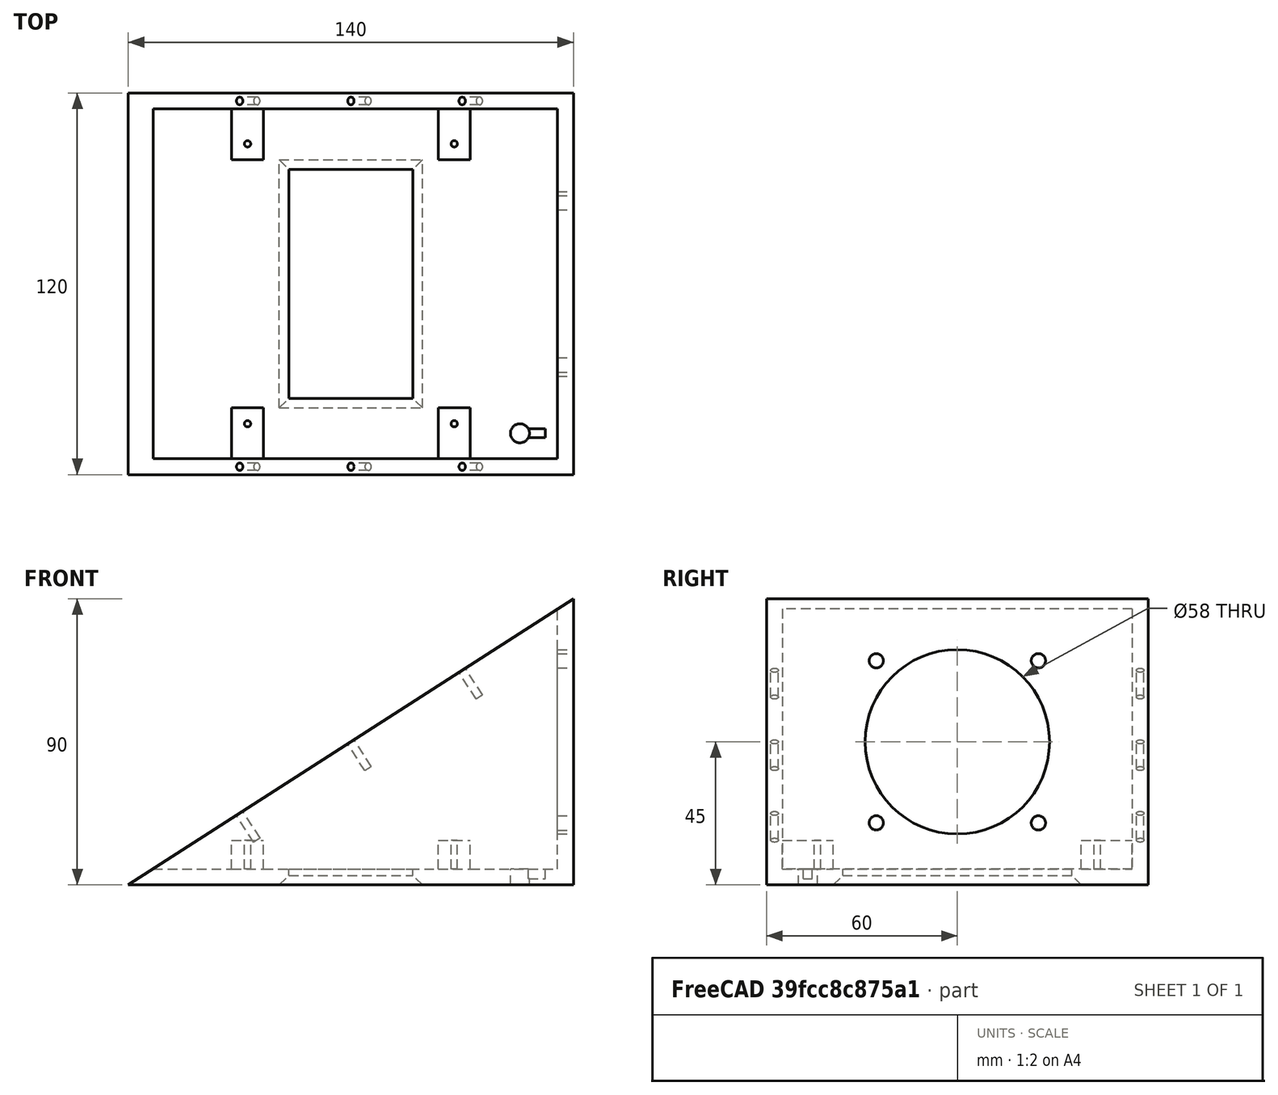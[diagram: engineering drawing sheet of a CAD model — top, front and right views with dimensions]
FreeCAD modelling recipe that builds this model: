
FCSTD DOCUMENT  (FreeCAD 0.19R22284 (Git))
Label: lcdmount
License: All rights reserved
LicenseURL: http://en.wikipedia.org/wiki/All_rights_reserved
objects: Part::Box×6, Part::Cylinder×5, Part::Cut×5, Part::MultiFuse×5, Part::Wedge×4, Part::FeaturePython×3, Sketcher::SketchObject×1, Spreadsheet::Sheet×1, Part::Chamfer×1, Mesh::Feature×1
note: 30 computed .brp shape members not serialized (recipe doc carries the construction recipe); baked Part::Feature solids carry a one-line shape summary decoded from their .brp

FEATURE [Sketcher::SketchObject] Sketch
  sketch-geometry (8):
    g0: LineSegment StartX=31.035 StartY=30.82 StartZ=0 EndX=-31.035 EndY=30.82 EndZ=0
    g1: LineSegment StartX=-31.035 StartY=30.82 StartZ=0 EndX=-31.035 EndY=-30.82 EndZ=0
    g2: LineSegment StartX=-31.035 StartY=-30.82 StartZ=0 EndX=31.035 EndY=-30.82 EndZ=0
    g3: LineSegment StartX=31.035 StartY=-30.82 StartZ=0 EndX=31.035 EndY=30.82 EndZ=0
    g4: LineSegment [constr] StartX=-21.915 StartY=21.365 StartZ=0 EndX=21.915 EndY=21.365 EndZ=0
    g5: LineSegment [constr] StartX=21.915 StartY=21.365 StartZ=0 EndX=21.915 EndY=-21.365 EndZ=0
    g6: LineSegment [constr] StartX=21.915 StartY=-21.365 StartZ=0 EndX=-21.915 EndY=-21.365 EndZ=0
    g7: LineSegment [constr] StartX=-21.915 StartY=-21.365 StartZ=0 EndX=-21.915 EndY=21.365 EndZ=0
  constraints (21):
    c: Coincident(g0,g1)
    c: Coincident(g1,g2)
    c: Coincident(g2,g3)
    c: Coincident(g3,g0)
    c: Horizontal(g0)
    c: Horizontal(g2)
    c: Vertical(g1)
    c: Vertical(g3)
    c: DistanceX(g0,g0) = 62.07  'extSizeX'
    c: DistanceY(g1,g1) = 61.64  'extSizeY'
    c: Symmetric(g0,g2,g-1)
    c: Coincident(g4,g5)
    c: Coincident(g5,g6)
    c: Coincident(g6,g7)
    c: Coincident(g7,g4)
    c: Horizontal(g4)
    c: Horizontal(g6)
    c: Vertical(g5)
    c: Vertical(g7)
    c: DistanceX(g4,g4) = 43.83  'LCDHoleOffsetX'
    c: DistanceY(g7,g7) = 42.73  'LCDHoleOffsetY'
FEATURE [Part::Box] Box001  label="lcdhole"
  AttacherType = Attacher::AttachEngine3D
  Height = 5
  Length = 39
  Placement = pos=(-19.5,-36,0) rot=(0,0,1;0rad)
  Width = 72
  expr: Height = Spreadsheet.mountThickness
  expr: Length = Spreadsheet.LCDSizeX
  expr: Width = Spreadsheet.LCDSizeY
  expr: .Placement.Base.x = Length / -2
  expr: .Placement.Base.y = Width / -2
FEATURE [Spreadsheet::Sheet] Spreadsheet
  cells = C2=X; D2=Y; E2=Z; B3=LCDSize; C3(LCDSizeX)==39mm; D3(LCDSizeY)==72mm; E3(LCDSizeZ)==9mm; B4=MountSize; C4(MountSizeX)==140mm; D4(MountSizeY)==110mm; A5=Position of mouting holes on LCD board; B5=LCDHoleOffset; C5(LCDHoleOffsetX)==65mm; D5(LCDHoleOffsetY)==88mm; B6=MountThickness; F6(mountThickness)==5mm; A7=Size of hole for the LCD screws; B7=LCDScrewHoleSize; F7(LCDScrewHoleSize)==1mm; A8=Size of the cylider the LCD will rest on top of, containing the screw hole; B8=LCDScrewHoleMountSize; F8(LCDScrewHoleMountSize)==5mm; A9=Length of the back part, when the fan mounts; B9=backLength; F9(backLength)==90mm; B10=angleA; G10(angleA)==atan(backLength / MountSizeX); B11=angleB; G11(angleB)==atan(MountSizeX / backLength); B12=fanRadius; G12(fanRadius)==29mm; B13=fanHoleSpacing; C13(fanHoleSpacingX)==51mm; D13(fanHoleSpacingY)==51mm; B14=fanScrewRadius; G14(fanScrewRadius)==2.25mm; B15=mountingHoleCount; C15(mountingHoleCountX)=3; B16=mountingHoleRadius; G16(mountingHoleRadius)==1.2mm; B17=mountingHoleDepth; G17(mountingHoleDepth)==10mm; B18=powerSwitchRadius; G18(powerSwitchRadius)==3mm; B19=powerSwitchSlotSize; C19(powerSwitchSlotSizeX)==2.75mm; D19(powerSwitchSlotSizeY)==8mm; E19(powerSwitchSlotSizeZ)==3mm
FEATURE [Part::Cylinder] Cylinder001  label="lcdScrewHoleInner"
  Angle = 360
  AttacherType = Attacher::AttachEngine3D
  Height = 12
  Placement = pos=(-32.5,-44,2) rot=(0,0,1;0rad)
  Radius = 1
  expr: .Placement.Base.x = Spreadsheet.LCDHoleOffsetX / -2
  expr: .Placement.Base.y = Spreadsheet.LCDHoleOffsetY / -2
  expr: .Placement.Base.z = 2mm
  expr: Height = Spreadsheet.LCDSizeZ + Spreadsheet.mountThickness - .Placement.Base.z
  expr: Radius = Spreadsheet.LCDScrewHoleSize
FEATURE [Part::Wedge] Wedge  label="backWedge"
  AttacherType = Attacher::AttachEngine3D
  Placement = pos=(65,0,0) rot=(0,0,-1;1.5708rad)
  X2max = 55
  X2min = -55
  Xmax = 55
  Xmin = -55
  Ymax = 5
  Ymin = 0
  Z2max = 90
  Z2min = 0
  Zmax = 86.7857
  Zmin = 0
  expr: .Placement.Base.x = Spreadsheet.MountSizeX / 2 - Spreadsheet.mountThickness
  expr: Ymax = Spreadsheet.mountThickness
  expr: Zmax = Spreadsheet.backLength - Spreadsheet.mountThickness / tan(Spreadsheet.angleB)
  expr: X2max = Spreadsheet.MountSizeY / 2
  expr: Xmin = -Spreadsheet.MountSizeY / 2
  expr: Xmax = Spreadsheet.MountSizeY / 2
  expr: X2min = -Spreadsheet.MountSizeY / 2
  expr: Z2max = Spreadsheet.backLength
FEATURE [Part::Wedge] Wedge001  label="lcdWedge"
  AttacherType = Attacher::AttachEngine3D
  Placement = pos=(0,0,0) rot=(1,0,0;1.5708rad)
  X2max = 70
  X2min = -62.2222
  Xmax = 70
  Xmin = -70
  Ymax = 5
  Ymin = 0
  Z2max = 55
  Z2min = -55
  Zmax = 55
  Zmin = -55
  expr: Ymax = Spreadsheet.mountThickness
  expr: Zmax = Spreadsheet.MountSizeY / 2
  expr: Z2max = Spreadsheet.MountSizeY / 2
  expr: Zmin = Spreadsheet.MountSizeY / -2
  expr: Z2min = Spreadsheet.MountSizeY / -2
  expr: X2max = Spreadsheet.MountSizeX / 2
  expr: Xmax = Spreadsheet.MountSizeX / 2
  expr: X2min = Xmin + Spreadsheet.mountThickness * tan(Spreadsheet.angleB)
  expr: Xmin = -Spreadsheet.MountSizeX / 2
FEATURE [Part::Cylinder] Cylinder002  label="fanAirHole"
  Angle = 360
  AttacherType = Attacher::AttachEngine3D
  Height = 5
  Placement = pos=(65,0,45) rot=(0,1,0;1.5708rad)
  Radius = 29
  expr: .Placement.Base.z = Spreadsheet.backLength / 2
  expr: Height = Spreadsheet.mountThickness
  expr: .Placement.Base.y = 0
  expr: .Placement.Base.x = Spreadsheet.MountSizeX / 2 - Spreadsheet.mountThickness
  expr: Radius = Spreadsheet.fanRadius
FEATURE [Part::Cylinder] Cylinder003  label="FanScrewHole"
  Angle = 360
  AttacherType = Attacher::AttachEngine3D
  Height = 5
  Placement = pos=(65,-25.5,19.5) rot=(0,1,0;1.5708rad)
  Radius = 2.25
  expr: .Placement.Base.x = <<fanAirHole>>.Placement.Base.x
  expr: .Placement.Base.y = <<fanAirHole>>.Placement.Base.y - Spreadsheet.fanHoleSpacingY / 2
  expr: .Placement.Base.z = <<fanAirHole>>.Placement.Base.z - Spreadsheet.fanHoleSpacingX / 2
  expr: Height = Spreadsheet.mountThickness
  expr: Radius = Spreadsheet.fanScrewRadius
FEATURE [Part::FeaturePython] Array001  label="fanScrewHoles"  # Draft array (typed FeaturePython)
  Angle = 360
  ArrayType = 0
  Axis = (0,0,1)
  Base = -> Cylinder003
  Center = (0,0,0)
  Fuse = false
  IntervalAxis = (0,0,0)
  IntervalX = (0,0,0)
  IntervalY = (0,51,0)
  IntervalZ = (0,0,51)
  NumberPolar = 1
  NumberX = 1
  NumberY = 2
  NumberZ = 2
  expr: .IntervalY.y = Spreadsheet.fanHoleSpacingX
  expr: .IntervalZ.z = Spreadsheet.fanHoleSpacingY
FEATURE [Part::Wedge] Wedge002  label="sideA"
  AttacherType = Attacher::AttachEngine3D
  Placement = pos=(0,0,0) rot=(0,0,1;1.5708rad)
  X2max = 60
  X2min = 55
  Xmax = 60
  Xmin = 55
  Ymax = 70
  Ymin = -70
  Z2max = 0
  Z2min = 0
  Zmax = 90
  Zmin = 0
  expr: Xmax = Spreadsheet.MountSizeY / 2 + Spreadsheet.mountThickness
  expr: X2min = Xmax - Spreadsheet.mountThickness
  expr: X2max = Spreadsheet.MountSizeY / 2 + Spreadsheet.mountThickness
  expr: Xmin = Xmax - Spreadsheet.mountThickness
  expr: Zmax = Spreadsheet.backLength
  expr: Ymax = Spreadsheet.MountSizeX / 2
  expr: Ymin = -Spreadsheet.MountSizeX / 2
FEATURE [Part::Wedge] Wedge003  label="sideB"
  AttacherType = Attacher::AttachEngine3D
  Placement = pos=(0,0,0) rot=(0,0,1;1.5708rad)
  X2max = -55
  X2min = -60
  Xmax = -55
  Xmin = -60
  Ymax = 70
  Ymin = -70
  Z2max = 0
  Z2min = 0
  Zmax = 90
  Zmin = 0
  expr: Xmin = -Spreadsheet.MountSizeY / 2 - Spreadsheet.mountThickness
  expr: X2min = -Spreadsheet.MountSizeY / 2 - Spreadsheet.mountThickness
  expr: Xmax = Xmin + Spreadsheet.mountThickness
  expr: X2max = Xmin + Spreadsheet.mountThickness
  expr: Ymin = -Spreadsheet.MountSizeX / 2
  expr: Ymax = Spreadsheet.MountSizeX / 2
  expr: Zmax = Spreadsheet.backLength
FEATURE [Part::Cut] Cut  label="lcdSide"
  Base = -> Wedge001
  Tool = -> Box001
FEATURE [Part::MultiFuse] Fusion  label="fanHoles"
  Shapes = -> [Cylinder002,Array001]
FEATURE [Part::Cut] Cut002  label="backSide"
  Base = -> Wedge
  Tool = -> Fusion
FEATURE [Part::Cylinder] Cylinder004  label="mountingHole"
  Angle = 360
  AttacherType = Attacher::AttachEngine3D
  Height = 10
  Placement = pos=(5.40758,0,-8.41178) rot=(0,-1,0;0.571337rad)
  Radius = 1.2
  expr: Radius = Spreadsheet.mountingHoleRadius
  expr: Height = Spreadsheet.mountingHoleDepth
  expr: .Placement.Base.z = -cos(Spreadsheet.angleA) * Height
  expr: .Placement.Rotation.Angle = Spreadsheet.angleA
  expr: .Placement.Base.x = sin(Spreadsheet.angleA) * Height
FEATURE [Part::FeaturePython] Array002  label="mountingHolesX"  # Draft array (typed FeaturePython)
  Angle = 360
  ArrayType = 0
  Axis = (0,0,1)
  Base = -> Cylinder004
  Center = (0,0,0)
  Fuse = false
  IntervalAxis = (0,0,0)
  IntervalX = (35,0,22.5)
  IntervalY = (0,115,0)
  IntervalZ = (0,0,1)
  NumberPolar = 1
  NumberX = 3
  NumberY = 2
  NumberZ = 0
  Placement = pos=(-35,-57.5,22.5) rot=(0,0,1;0rad)
  expr: NumberX = Spreadsheet.mountingHoleCountX
  expr: .IntervalX.x = Spreadsheet.MountSizeX / (Spreadsheet.mountingHoleCountX + 1)
  expr: .IntervalY.y = Spreadsheet.MountSizeY + Spreadsheet.mountThickness
  expr: .Placement.Base.x = -Spreadsheet.MountSizeX / (Spreadsheet.mountingHoleCountX + 1)
  expr: .Placement.Base.y = -.IntervalY.y / 2
  expr: .Placement.Base.z = Spreadsheet.backLength / (Spreadsheet.mountingHoleCountX + 1)
  expr: .IntervalX.z = Spreadsheet.backLength / (Spreadsheet.mountingHoleCountX + 1)
FEATURE [Part::MultiFuse] Fusion001  label="sides"
  Shapes = -> [Wedge002,Wedge003]
FEATURE [Part::Cut] Cut003  label="sidesWithHoles"
  Base = -> Fusion001
  Tool = -> Array002
FEATURE [Part::Chamfer] Chamfer  label="lcdFaceWithChamfer"
  Base = -> Cut
  Edges = 4 edges r=3: [Edge8,Edge9,Edge10,Edge11]
FEATURE [Part::Box] Box  label="lcdMountA"
  AttacherType = Attacher::AttachEngine3D
  Height = 9
  Length = 10
  Placement = pos=(-37.5,39,5) rot=(0,0,1;0rad)
  Width = 16
  expr: Length = 2 * Spreadsheet.LCDScrewHoleMountSize
  expr: .Placement.Base.x = Spreadsheet.LCDHoleOffsetX / -2 - Spreadsheet.LCDScrewHoleMountSize
  expr: .Placement.Base.y = Spreadsheet.LCDHoleOffsetY / 2 - Spreadsheet.LCDScrewHoleMountSize
  expr: Width = Spreadsheet.MountSizeY / 2 - .Placement.Base.y
  expr: Height = Spreadsheet.LCDSizeZ
  expr: .Placement.Base.z = Spreadsheet.mountThickness
FEATURE [Part::Box] Box002  label="lcdMountB"
  AttacherType = Attacher::AttachEngine3D
  Height = 9
  Length = 10
  Placement = pos=(27.5,39,5) rot=(0,0,1;0rad)
  Width = 16
  expr: Length = 2 * Spreadsheet.LCDScrewHoleMountSize
  expr: .Placement.Base.x = Spreadsheet.LCDHoleOffsetX / 2 - Spreadsheet.LCDScrewHoleMountSize
  expr: .Placement.Base.y = Spreadsheet.LCDHoleOffsetY / 2 - Spreadsheet.LCDScrewHoleMountSize
  expr: Width = Spreadsheet.MountSizeY / 2 - .Placement.Base.y
  expr: Height = Spreadsheet.LCDSizeZ
  expr: .Placement.Base.z = Spreadsheet.mountThickness
FEATURE [Part::Box] Box003  label="lcdMountC"
  AttacherType = Attacher::AttachEngine3D
  Height = 9
  Length = 10
  Placement = pos=(27.5,-55,5) rot=(0,0,1;0rad)
  Width = 16
  expr: Length = 2 * Spreadsheet.LCDScrewHoleMountSize
  expr: .Placement.Base.x = Spreadsheet.LCDHoleOffsetX / 2 - Spreadsheet.LCDScrewHoleMountSize
  expr: .Placement.Base.y = Spreadsheet.MountSizeY / -2
  expr: Width = Spreadsheet.MountSizeY / 2 - Spreadsheet.LCDHoleOffsetY / 2 + Spreadsheet.LCDScrewHoleMountSize
  expr: Height = Spreadsheet.LCDSizeZ
  expr: .Placement.Base.z = Spreadsheet.mountThickness
FEATURE [Part::Box] Box004  label="lcdMountD"
  AttacherType = Attacher::AttachEngine3D
  Height = 9
  Length = 10
  Placement = pos=(-37.5,-55,5) rot=(0,0,1;0rad)
  Width = 16
  expr: Length = 2 * Spreadsheet.LCDScrewHoleMountSize
  expr: .Placement.Base.x = Spreadsheet.LCDHoleOffsetX / -2 - Spreadsheet.LCDScrewHoleMountSize
  expr: .Placement.Base.y = Spreadsheet.MountSizeY / -2
  expr: Width = Spreadsheet.MountSizeY / 2 - Spreadsheet.LCDHoleOffsetY / 2 + Spreadsheet.LCDScrewHoleMountSize
  expr: Height = Spreadsheet.LCDSizeZ
  expr: .Placement.Base.z = Spreadsheet.mountThickness
FEATURE [Part::FeaturePython] Array  label="lcdMountHoleArray"  # Draft array (typed FeaturePython)
  Angle = 360
  ArrayType = 0
  Axis = (0,0,1)
  Base = -> Cylinder001
  Center = (0,0,0)
  Fuse = false
  IntervalAxis = (0,0,0)
  IntervalX = (65,0,0)
  IntervalY = (0,88,0)
  IntervalZ = (0,0,1)
  NumberPolar = 1
  NumberX = 2
  NumberY = 2
  NumberZ = 1
  expr: .IntervalX.x = Spreadsheet.LCDHoleOffsetX
  expr: .IntervalY.y = Spreadsheet.LCDHoleOffsetY
FEATURE [Part::MultiFuse] Fusion003  label="lcdMountOuters"
  Shapes = -> [Box004,Box003,Box002,Box]
FEATURE [Part::Cut] Cut004  label="lcdMounts"
  Base = -> Fusion003
  Tool = -> Array
FEATURE [Part::Cylinder] Cylinder  label="powerSwitchDrill"
  Angle = 360
  AttacherType = Attacher::AttachEngine3D
  Height = 5
  Radius = 3
  expr: Radius = Spreadsheet.powerSwitchRadius
  expr: Height = Spreadsheet.mountThickness
FEATURE [Part::Box] Box005  label="powerSwitchAlignmentSlot"
  AttacherType = Attacher::AttachEngine3D
  Height = 3
  Length = 8
  Placement = pos=(0,-1.375,2) rot=(0,0,1;0rad)
  Width = 2.75
  expr: Width = Spreadsheet.powerSwitchSlotSizeX
  expr: Height = Spreadsheet.powerSwitchSlotSizeZ
  expr: .Placement.Base.z = Spreadsheet.mountThickness - Height
  expr: Length = Spreadsheet.powerSwitchSlotSizeY
  expr: .Placement.Base.x = 0
  expr: .Placement.Base.y = Width / -2
FEATURE [Part::MultiFuse] Fusion004  label="powerSwitch"
  Placement = pos=(53.1667,-47,0) rot=(0,0,1;0rad)
  Shapes = -> [Cylinder,Box005]
  expr: .Placement.Base.y = (Spreadsheet.MountSizeY - Spreadsheet.LCDSizeY + Spreadsheet.LCDSizeY / 2 / 4) * -1
  expr: .Placement.Base.x = (Spreadsheet.MountSizeX - Spreadsheet.LCDSizeX) / 2 / 1.5 + Spreadsheet.LCDSizeX / 2
FEATURE [Part::Cut] Cut005  label="lcdFace"
  Base = -> Chamfer
  Tool = -> Fusion004
FEATURE [Part::MultiFuse] Fusion002  label="model"
  Shapes = -> [Cut002,Cut003,Cut004,Cut005]
FEATURE [Mesh::Feature] Mesh  label="model (Meshed)"
